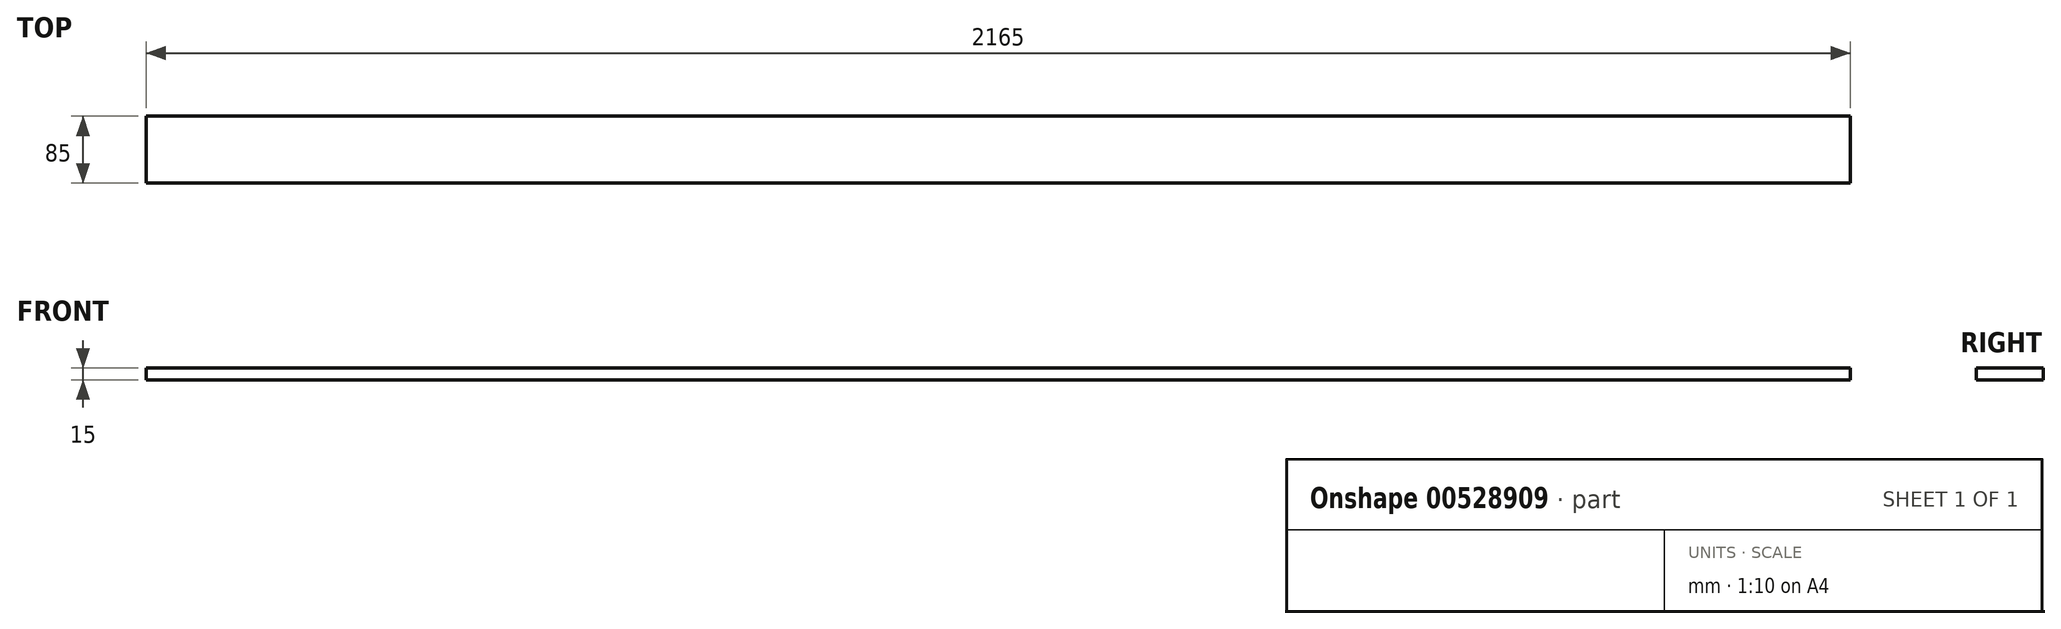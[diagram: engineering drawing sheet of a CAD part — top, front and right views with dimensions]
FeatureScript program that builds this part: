
annotation { "Feature Type Name" : "Feature", "Feature Type Description" : "" }
export const myFeature = defineFeature(function(context is Context, id is Id, definition is map)
    precondition{}
    {
        {
            var Q0;
            Q0=qCreatedBy(makeId("Right.planeOp"),FACE);
            var sketch = newSketch(context, id + "F0", { "sketchPlane" : qUnion([Q0])});
            skLineSegment(sketch, "E0.bottom", {"start": v(0, 0) * mm, "end": v(85, 0) * mm});
            skLineSegment(sketch, "E0.top", {"start": v(0, 15) * mm, "end": v(85, 15) * mm});
            skLineSegment(sketch, "E0.left", {"start": v(0, 0) * mm, "end": v(0, 15) * mm});
            skLineSegment(sketch, "E0.right", {"start": v(85, 0) * mm, "end": v(85, 15) * mm});
            skSolve(sketch);
        }
        {
            var Q0;
            Q0 = qSketchRegion(id + "F0", true);
            extrude(context, id + "F1", {"entities" : qUnion([Q0]), "endBound" : BoundingType.SYMMETRIC, "depth" : 2165 * mm, "offsetDistance" : 25 * mm});
        }
    });
